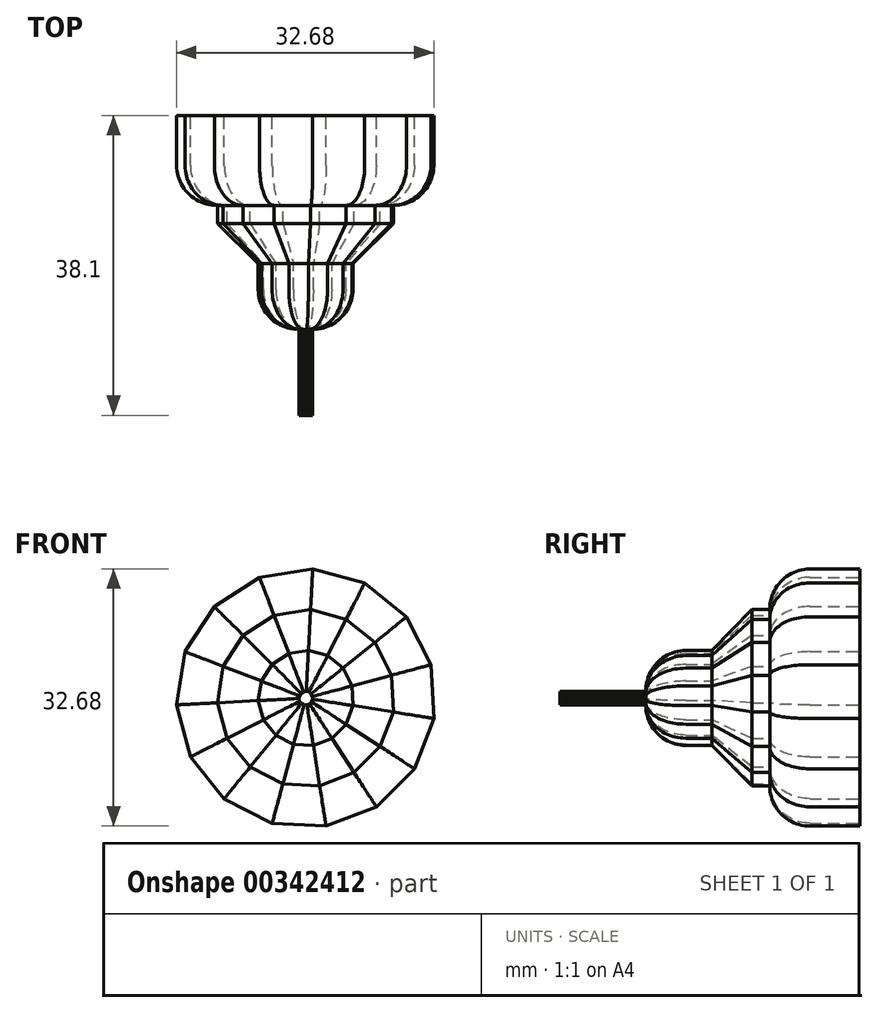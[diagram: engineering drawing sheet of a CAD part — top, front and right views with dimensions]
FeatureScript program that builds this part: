
annotation { "Feature Type Name" : "Feature", "Feature Type Description" : "" }
export const myFeature = defineFeature(function(context is Context, id is Id, definition is map)
    precondition{}
    {
        {
            var Q0;
            Q0=qCreatedBy(makeId("Front.planeOp"),FACE);
            var sketch = newSketch(context, id + "F0", { "sketchPlane" : qUnion([Q0])});
            skCircle(sketch, "E0.cCircle", {"center": v(0, 0) * mm, "radius": 16.1 * mm, "construction": true});
            skLineSegment(sketch, "E0.0", {"start": v(-11.62, 11.64) * mm, "end": v(-5.88, 15.36) * mm});
            skLineSegment(sketch, "E0.1", {"start": v(-5.88, 15.36) * mm, "end": v(0.87, 16.43) * mm});
            skLineSegment(sketch, "E0.2", {"start": v(0.87, 16.43) * mm, "end": v(7.48, 14.65) * mm});
            skLineSegment(sketch, "E0.3", {"start": v(7.48, 14.65) * mm, "end": v(12.8, 10.34) * mm});
            skLineSegment(sketch, "E0.4", {"start": v(12.8, 10.34) * mm, "end": v(15.9, 4.25) * mm});
            skLineSegment(sketch, "E0.5", {"start": v(15.9, 4.25) * mm, "end": v(16.25, -2.58) * mm});
            skLineSegment(sketch, "E0.6", {"start": v(16.25, -2.58) * mm, "end": v(13.8, -8.97) * mm});
            skLineSegment(sketch, "E0.7", {"start": v(13.8, -8.97) * mm, "end": v(8.95, -13.8) * mm});
            skLineSegment(sketch, "E0.8", {"start": v(8.95, -13.8) * mm, "end": v(2.56, -16.25) * mm});
            skLineSegment(sketch, "E0.9", {"start": v(2.56, -16.25) * mm, "end": v(-4.27, -15.89) * mm});
            skLineSegment(sketch, "E0.10", {"start": v(-4.27, -15.89) * mm, "end": v(-10.36, -12.78) * mm});
            skLineSegment(sketch, "E0.11", {"start": v(-10.36, -12.78) * mm, "end": v(-14.66, -7.46) * mm});
            skLineSegment(sketch, "E0.12", {"start": v(-14.66, -7.46) * mm, "end": v(-16.43, -0.85) * mm});
            skLineSegment(sketch, "E0.13", {"start": v(-16.43, -0.85) * mm, "end": v(-15.35, 5.9) * mm});
            skLineSegment(sketch, "E0.14", {"start": v(-15.35, 5.9) * mm, "end": v(-11.62, 11.64) * mm});
            skPoint(sketch, "E0.0.midPoint", {"position": v(-8.75, 13.5) * mm});
            skSolve(sketch);
        }
        {
            var Q0;
            Q0 = qSketchRegion(id + "F0", true);
            extrude(context, id + "F1", {"entities" : qUnion([Q0]), "depth" : 11.43 * mm});
        }
        {
            var Q0;
            Q0=makeQuery(id+"F1.opExtrude","CAP_FACE",FACE,{"disambiguationData":[OSD([sQuery(id+"F0.wireOp",EDGE,"E0.0"),sQuery(id+"F0.wireOp",EDGE,"E0.1"),sQuery(id+"F0.wireOp",EDGE,"E0.2"),sQuery(id+"F0.wireOp",EDGE,"E0.3"),sQuery(id+"F0.wireOp",EDGE,"E0.4"),sQuery(id+"F0.wireOp",EDGE,"E0.5"),sQuery(id+"F0.wireOp",EDGE,"E0.6"),sQuery(id+"F0.wireOp",EDGE,"E0.7"),sQuery(id+"F0.wireOp",EDGE,"E0.8"),sQuery(id+"F0.wireOp",EDGE,"E0.9"),sQuery(id+"F0.wireOp",EDGE,"E0.10"),sQuery(id+"F0.wireOp",EDGE,"E0.11"),sQuery(id+"F0.wireOp",EDGE,"E0.12"),sQuery(id+"F0.wireOp",EDGE,"E0.13"),sQuery(id+"F0.wireOp",EDGE,"E0.14")])],"isStart":false});
            fillet(context, id + "F2", {"entities" : qUnion([Q0]), "radius" : 5.08 * mm, "tangentPropagation" : true, "allowEdgeOverflow" : false});
        }
        {
            var Q0;
            Q0=makeQuery(id+"F1.opExtrude","CAP_FACE",FACE,{"disambiguationData":[OSD([sQuery(id+"F0.wireOp",EDGE,"E0.0"),sQuery(id+"F0.wireOp",EDGE,"E0.1"),sQuery(id+"F0.wireOp",EDGE,"E0.2"),sQuery(id+"F0.wireOp",EDGE,"E0.3"),sQuery(id+"F0.wireOp",EDGE,"E0.4"),sQuery(id+"F0.wireOp",EDGE,"E0.5"),sQuery(id+"F0.wireOp",EDGE,"E0.6"),sQuery(id+"F0.wireOp",EDGE,"E0.7"),sQuery(id+"F0.wireOp",EDGE,"E0.8"),sQuery(id+"F0.wireOp",EDGE,"E0.9"),sQuery(id+"F0.wireOp",EDGE,"E0.10"),sQuery(id+"F0.wireOp",EDGE,"E0.11"),sQuery(id+"F0.wireOp",EDGE,"E0.12"),sQuery(id+"F0.wireOp",EDGE,"E0.13"),sQuery(id+"F0.wireOp",EDGE,"E0.14")])],"isStart":false});
            extrude(context, id + "F3", {"entities" : qUnion([Q0]), "operationType" : NewBodyOperationType.ADD, "depth" : 2.3 * mm});
        }
        {
            var Q0;
            Q0=makeQuery(id+"F3.opExtrude","CAP_FACE",FACE,{"disambiguationData":[OSD([sQuery(id+"F0.wireOp",EDGE,"E0.0"),sQuery(id+"F0.wireOp",EDGE,"E0.1"),sQuery(id+"F0.wireOp",EDGE,"E0.2"),sQuery(id+"F0.wireOp",EDGE,"E0.3"),sQuery(id+"F0.wireOp",EDGE,"E0.4"),sQuery(id+"F0.wireOp",EDGE,"E0.5"),sQuery(id+"F0.wireOp",EDGE,"E0.6"),sQuery(id+"F0.wireOp",EDGE,"E0.7"),sQuery(id+"F0.wireOp",EDGE,"E0.8"),sQuery(id+"F0.wireOp",EDGE,"E0.9"),sQuery(id+"F0.wireOp",EDGE,"E0.10"),sQuery(id+"F0.wireOp",EDGE,"E0.11"),sQuery(id+"F0.wireOp",EDGE,"E0.12"),sQuery(id+"F0.wireOp",EDGE,"E0.13"),sQuery(id+"F0.wireOp",EDGE,"E0.14")])],"isStart":false});
            extrude(context, id + "F4", {"entities" : qUnion([Q0]), "operationType" : NewBodyOperationType.ADD, "depth" : 5.08 * mm});
        }
        {
            var Q0;
            {var subQ0=sQuery(id+"F0.wireOp",EDGE,"E0.14");var subQ1=sQuery(id+"F0.wireOp",EDGE,"E0.13");var subQ2=sQuery(id+"F0.wireOp",EDGE,"E0.12");var subQ3=sQuery(id+"F0.wireOp",EDGE,"E0.11");var subQ4=sQuery(id+"F0.wireOp",EDGE,"E0.10");var subQ5=sQuery(id+"F0.wireOp",EDGE,"E0.9");var subQ6=sQuery(id+"F0.wireOp",EDGE,"E0.8");var subQ7=sQuery(id+"F0.wireOp",EDGE,"E0.7");var subQ8=sQuery(id+"F0.wireOp",EDGE,"E0.6");var subQ9=sQuery(id+"F0.wireOp",EDGE,"E0.5");var subQ10=sQuery(id+"F0.wireOp",EDGE,"E0.4");var subQ11=sQuery(id+"F0.wireOp",EDGE,"E0.3");var subQ12=sQuery(id+"F0.wireOp",EDGE,"E0.2");var subQ13=sQuery(id+"F0.wireOp",EDGE,"E0.1");var subQ14=sQuery(id+"F0.wireOp",EDGE,"E0.0");Q0=makeQuery(id+"F4.opExtrude","CAP_EDGE",EDGE,{"disambiguationData":[OSD([subQ14,subQ13,subQ12,subQ11,subQ10,subQ9,subQ8,subQ7,subQ6,subQ5,subQ4,subQ3,subQ2,subQ1,subQ0]),TDD([makeQuery(id+"F3.opExtrude","CAP_EDGE",EDGE,{"disambiguationData":[OSD([subQ14,subQ13,subQ12,subQ11,subQ10,subQ9,subQ8,subQ7,subQ6,subQ5,subQ4,subQ3,subQ2,subQ1,subQ0]),TDD([makeQuery(id+"F2.opFillet","BLEND_EDGE",EDGE,{"blendedFrom":[makeQuery(id+"F1.opExtrude","CAP_EDGE",EDGE,{"disambiguationData":[OSD([subQ5])],"isStart":false}),makeQuery(id+"F1.opExtrude","CAP_FACE",FACE,{"disambiguationData":[OSD([subQ14,subQ13,subQ12,subQ11,subQ10,subQ9,subQ8,subQ7,subQ6,subQ5,subQ4,subQ3,subQ2,subQ1,subQ0])],"isStart":false})],"blendedInto":[makeQuery(id+"F1.opExtrude","CAP_FACE",FACE,{"disambiguationData":[OSD([subQ14,subQ13,subQ12,subQ11,subQ10,subQ9,subQ8,subQ7,subQ6,subQ5,subQ4,subQ3,subQ2,subQ1,subQ0])],"isStart":false})]})])],"isStart":false})])],"isStart":false});}
            var Q1;
            Q1=makeQuery(id+"F4.opExtrude","CAP_FACE",FACE,{"disambiguationData":[OSD([sQuery(id+"F0.wireOp",EDGE,"E0.0"),sQuery(id+"F0.wireOp",EDGE,"E0.1"),sQuery(id+"F0.wireOp",EDGE,"E0.2"),sQuery(id+"F0.wireOp",EDGE,"E0.3"),sQuery(id+"F0.wireOp",EDGE,"E0.4"),sQuery(id+"F0.wireOp",EDGE,"E0.5"),sQuery(id+"F0.wireOp",EDGE,"E0.6"),sQuery(id+"F0.wireOp",EDGE,"E0.7"),sQuery(id+"F0.wireOp",EDGE,"E0.8"),sQuery(id+"F0.wireOp",EDGE,"E0.9"),sQuery(id+"F0.wireOp",EDGE,"E0.10"),sQuery(id+"F0.wireOp",EDGE,"E0.11"),sQuery(id+"F0.wireOp",EDGE,"E0.12"),sQuery(id+"F0.wireOp",EDGE,"E0.13"),sQuery(id+"F0.wireOp",EDGE,"E0.14")])],"isStart":false});
            chamfer(context, id + "F5", {"entities" : qUnion([Q0, Q1]), "width" : 5.08 * mm, "tangentPropagation" : true});
        }
        {
            var Q0;
            Q0=makeQuery(id+"F4.opExtrude","CAP_FACE",FACE,{"disambiguationData":[OSD([sQuery(id+"F0.wireOp",EDGE,"E0.0"),sQuery(id+"F0.wireOp",EDGE,"E0.1"),sQuery(id+"F0.wireOp",EDGE,"E0.2"),sQuery(id+"F0.wireOp",EDGE,"E0.3"),sQuery(id+"F0.wireOp",EDGE,"E0.4"),sQuery(id+"F0.wireOp",EDGE,"E0.5"),sQuery(id+"F0.wireOp",EDGE,"E0.6"),sQuery(id+"F0.wireOp",EDGE,"E0.7"),sQuery(id+"F0.wireOp",EDGE,"E0.8"),sQuery(id+"F0.wireOp",EDGE,"E0.9"),sQuery(id+"F0.wireOp",EDGE,"E0.10"),sQuery(id+"F0.wireOp",EDGE,"E0.11"),sQuery(id+"F0.wireOp",EDGE,"E0.12"),sQuery(id+"F0.wireOp",EDGE,"E0.13"),sQuery(id+"F0.wireOp",EDGE,"E0.14")])],"isStart":false});
            extrude(context, id + "F6", {"entities" : qUnion([Q0]), "operationType" : NewBodyOperationType.ADD, "depth" : 8.38 * mm});
        }
        {
            var Q0;
            Q0=makeQuery(id+"F6.opExtrude","CAP_FACE",FACE,{"disambiguationData":[OSD([sQuery(id+"F0.wireOp",EDGE,"E0.0"),sQuery(id+"F0.wireOp",EDGE,"E0.1"),sQuery(id+"F0.wireOp",EDGE,"E0.2"),sQuery(id+"F0.wireOp",EDGE,"E0.3"),sQuery(id+"F0.wireOp",EDGE,"E0.4"),sQuery(id+"F0.wireOp",EDGE,"E0.5"),sQuery(id+"F0.wireOp",EDGE,"E0.6"),sQuery(id+"F0.wireOp",EDGE,"E0.7"),sQuery(id+"F0.wireOp",EDGE,"E0.8"),sQuery(id+"F0.wireOp",EDGE,"E0.9"),sQuery(id+"F0.wireOp",EDGE,"E0.10"),sQuery(id+"F0.wireOp",EDGE,"E0.11"),sQuery(id+"F0.wireOp",EDGE,"E0.12"),sQuery(id+"F0.wireOp",EDGE,"E0.13"),sQuery(id+"F0.wireOp",EDGE,"E0.14")])],"isStart":false});
            fillet(context, id + "F7", {"entities" : qUnion([Q0]), "radius" : 5.08 * mm, "tangentPropagation" : true, "allowEdgeOverflow" : false});
        }
        {
            var Q0;
            Q0=makeQuery(id+"F6.opExtrude","CAP_FACE",FACE,{"disambiguationData":[OSD([sQuery(id+"F0.wireOp",EDGE,"E0.0"),sQuery(id+"F0.wireOp",EDGE,"E0.1"),sQuery(id+"F0.wireOp",EDGE,"E0.2"),sQuery(id+"F0.wireOp",EDGE,"E0.3"),sQuery(id+"F0.wireOp",EDGE,"E0.4"),sQuery(id+"F0.wireOp",EDGE,"E0.5"),sQuery(id+"F0.wireOp",EDGE,"E0.6"),sQuery(id+"F0.wireOp",EDGE,"E0.7"),sQuery(id+"F0.wireOp",EDGE,"E0.8"),sQuery(id+"F0.wireOp",EDGE,"E0.9"),sQuery(id+"F0.wireOp",EDGE,"E0.10"),sQuery(id+"F0.wireOp",EDGE,"E0.11"),sQuery(id+"F0.wireOp",EDGE,"E0.12"),sQuery(id+"F0.wireOp",EDGE,"E0.13"),sQuery(id+"F0.wireOp",EDGE,"E0.14")])],"isStart":false});
            extrude(context, id + "F8", {"entities" : qUnion([Q0]), "operationType" : NewBodyOperationType.ADD, "depth" : 10.92 * mm});
        }
    });
